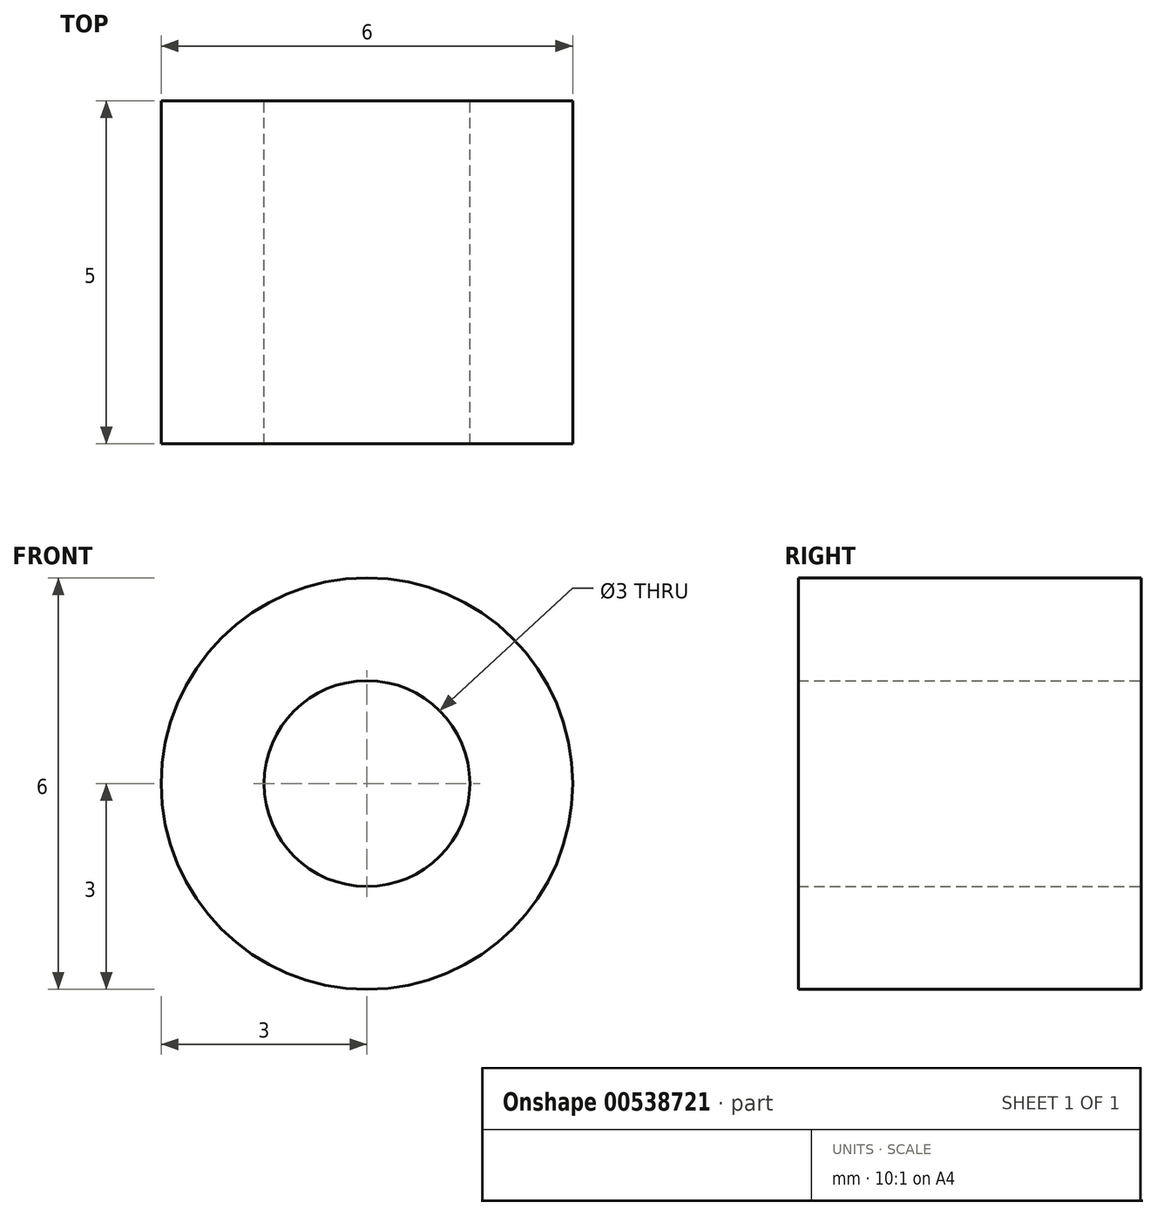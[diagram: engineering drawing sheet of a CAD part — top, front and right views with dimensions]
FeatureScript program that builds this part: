
annotation { "Feature Type Name" : "Feature", "Feature Type Description" : "" }
export const myFeature = defineFeature(function(context is Context, id is Id, definition is map)
    precondition{}
    {
        {
            var Q0;
            Q0=qCreatedBy(makeId("Front.planeOp"),FACE);
            var sketch = newSketch(context, id + "F0", { "sketchPlane" : qUnion([Q0])});
            skCircle(sketch, "E0", {"center": v(0, 0) * mm, "radius": 1.5 * mm});
            skCircle(sketch, "E1", {"center": v(0, 0) * mm, "radius": 3 * mm});
            skSolve(sketch);
        }
        {
            var Q0;
            Q0=makeQuery(id+"F0.imprint","IMPRINT",FACE,{"disambiguationData":[TD([[makeQuery(id+"F0.imprint","IMPRINT",EDGE,{"derivedFrom":sQuery(id+"F0.wireOp",EDGE,"E0")}),-1.0]])]});
            extrude(context, id + "F1", {"entities" : qUnion([Q0]), "depth" : 5 * mm, "offsetDistance" : 25 * mm});
        }
    });
